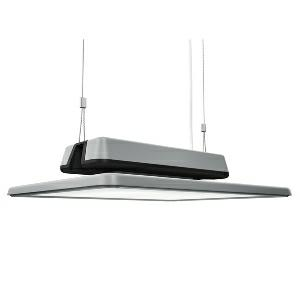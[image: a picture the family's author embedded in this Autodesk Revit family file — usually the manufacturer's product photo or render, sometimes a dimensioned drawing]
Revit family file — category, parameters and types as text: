
# Revit family: acaneo_-_hial_14000_850_n_ea_00737251_19ce
name_source: partatom
category: Lighting Fixtures
units: mm (PartAtom-declared; Revit-internal decimal feet)

## family parameters
Cut with Voids When Loaded = No
Host = Face
Light Source = No
Part Type = Normal
Room Calculation Point = No
Round Connector Dimension = Use Diameter
Shared = No

## types (1)
- ACANEO - HIAL 14000/850/N/EA (1 x LED, 15000 lm, 5000K)
    Apparent Load = 90 VA
    Approval mark = CE
    CIE Flux Codes = 84 97 100 100 100
    Color Rendering = 80-89
    Color Temperature = 5000K
    Control Gear = Electronic ballast
    Default Elevation = 1800 mm
    Description = HIAL 14000/850/N/EA|High bay luminaire|light source: LED|work equipment: Electronic ballast|connected load: 220-240 V, 50/60 Hz|Power consumption: approx. 90 W|power factor: approx. 0,950|luminous flux: 15000 lm|luminous efficacy: 166 lm/W|colour temperature: Cold white, ca. 5000 K|color rendering index (CRI): >= 80|chromaticity tolerance:  3 SDCM|System of protection: IP 65|class of protection: I|technology: Switchable|luminaire body|material: Aluminium|surface: Powder coatet|colour: White aluminium|lamp cover: Acrylic (PMMA), Clear|weight (net): approx. 8.2 kg|mains lead: Built-in plug RST 25i3 Einbau|Fastening: Available separately|Accessory: Junction box (RST 2013)|minimum ambient temperature: -30 ░C|maximum ambient temperature: 50 ░C|glare control: Optics|unified glare rating(4H 8H): <=  19|
    Frequency = 50 Hz, 60 Hz
    Height = 125 mm
    Lamp = 1 x LED
    Lamp Light Flux = 15000 lm
    Lamp count = 1
    Length = 480 mm
    Luminous efficacy = 167 lm/W
    Manufacturer = Waldmann
    ModVariant = No
    Model = 00737251
    Mounting Place = Ceiling
    Mounting Type = Pendant
    Number of Poles = 1
    OnlyDefault = Yes
    Power Factor = 1
    Product Name = ACANEO - HIAL 14000/850/N/EA
    Product group = High bay luminaire (industry)
    ProductGroupID = 901
    Protection Class = Protection class I
    Protection Degree = IP 65
    RLX_Detail_Level = 1
    RLX_Emergency_Light_Flux = 0 lm
    RLX_Emergency_Type = 0
    RLX_Emergency_Type_DB = No
    RlxData = <blob elided: 30293 chars, md5=57935f43>
    Socket = socket
    Standby Power = 0 W
    System Light Flux = 15000 lm
    System Power = 90 W
    Type Comments = Product without accessories
    Type Image = acaneo-hial.jpg
    URL = http://relux.com
    VarID = ---
    Voltage = 230 V
    Voltage Range = 110-120 V, 220-240 V
    Weight = 0.00 kg
    Width = 405 mm

## geometry (parser evidence)
native form markers: Blend x4, Sweep x9
no freeform markers — native parametric forms only
